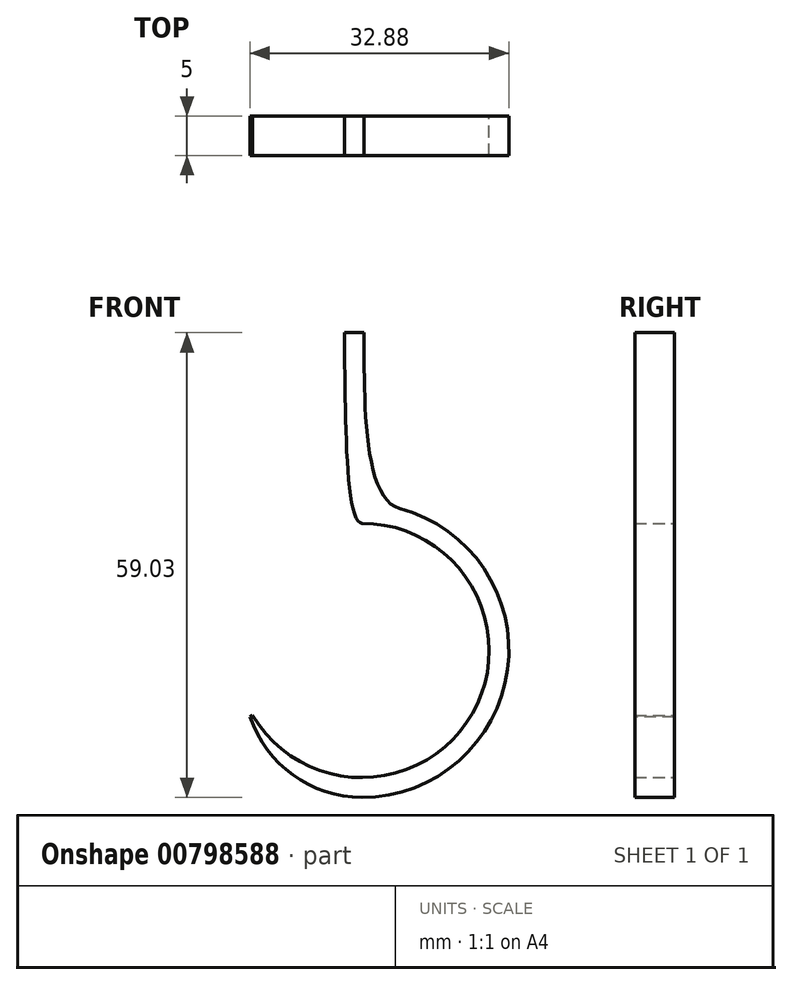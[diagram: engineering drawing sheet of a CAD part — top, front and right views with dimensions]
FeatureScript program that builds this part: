
annotation { "Feature Type Name" : "Feature", "Feature Type Description" : "" }
export const myFeature = defineFeature(function(context is Context, id is Id, definition is map)
    precondition{}
    {
        {
            var Q0;
            Q0=qCreatedBy(makeId("Front.planeOp"),FACE);
            var sketch = newSketch(context, id + "F0", { "sketchPlane" : qUnion([Q0])});
            skArc(sketch, "E0", {"start": v(0, 16.16) * mm, "mid": v(14.04, -8) * mm, "end": v(-13.9, -8.24) * mm});
            skArc(sketch, "E1", {"start": v(4.78, 18.03) * mm, "mid": v(14.88, -11.25) * mm, "end": v(-16.05, -9.52) * mm});
            skLineSegment(sketch, "E2", {"start": v(-16.05, -9.52) * mm, "end": v(-13.9, -8.24) * mm});
            skLineSegment(sketch, "E3", {"start": v(-13.9, -8.24) * mm, "end": v(-16.33, -4.15) * mm, "construction": true});
            skFitSpline(sketch, "E4", {"points": [v(4.78, 18.03) * mm, v(0.25, 40.37) * mm], "startDerivative": vector(-14.35, 3.8) * mm, "endDerivative": vector(-0.17, 23.92) * mm});
            skFitSpline(sketch, "E5", {"points": [v(0, 16.16) * mm, v(-2.25, 40.37) * mm], "startDerivative": vector(-6.72, 0) * mm, "endDerivative": vector(-0.48, 28.79) * mm});
            skLineSegment(sketch, "E6", {"start": v(-2.25, 40.37) * mm, "end": v(0.25, 40.37) * mm});
            skSolve(sketch);
        }
        {
            var Q0;
            Q0 = qSketchRegion(id + "F0", true);
            extrude(context, id + "F1", {"entities" : qUnion([Q0]), "endBound" : BoundingType.SYMMETRIC, "depth" : 5 * mm, "offsetDistance" : 25 * mm});
        }
        {
            var Q0;
            Q0=makeQuery(id+"F1.opExtrude","SWEPT_EDGE",EDGE,{"disambiguationData":[OSD([sQuery(id+"F0.wireOp",EDGE,"E1"),sQuery(id+"F0.wireOp",EDGE,"E2")])]});
            chamfer(context, id + "F2", {"entities" : qUnion([Q0]), "width" : 2 * mm, "tangentPropagation" : true});
        }
        {
            var Q0;
            {var subQ0=sQuery(id+"F0.wireOp",EDGE,"E1");Q0=makeQuery(id+"F2.opChamfer","BLEND_EDGE",EDGE,{"blendedFrom":[makeQuery(id+"F1.opExtrude","SWEPT_EDGE",EDGE,{"disambiguationData":[OSD([subQ0,sQuery(id+"F0.wireOp",EDGE,"E2")])]}),makeQuery(id+"F1.opExtrude","SWEPT_FACE",FACE,{"disambiguationData":[OSD([subQ0])]})],"blendedInto":[makeQuery(id+"F1.opExtrude","SWEPT_FACE",FACE,{"disambiguationData":[OSD([subQ0])]})]});}
            fillet(context, id + "F3", {"entities" : qUnion([Q0]), "radius" : 15 * mm, "tangentPropagation" : true, "allowEdgeOverflow" : false});
        }
    });
